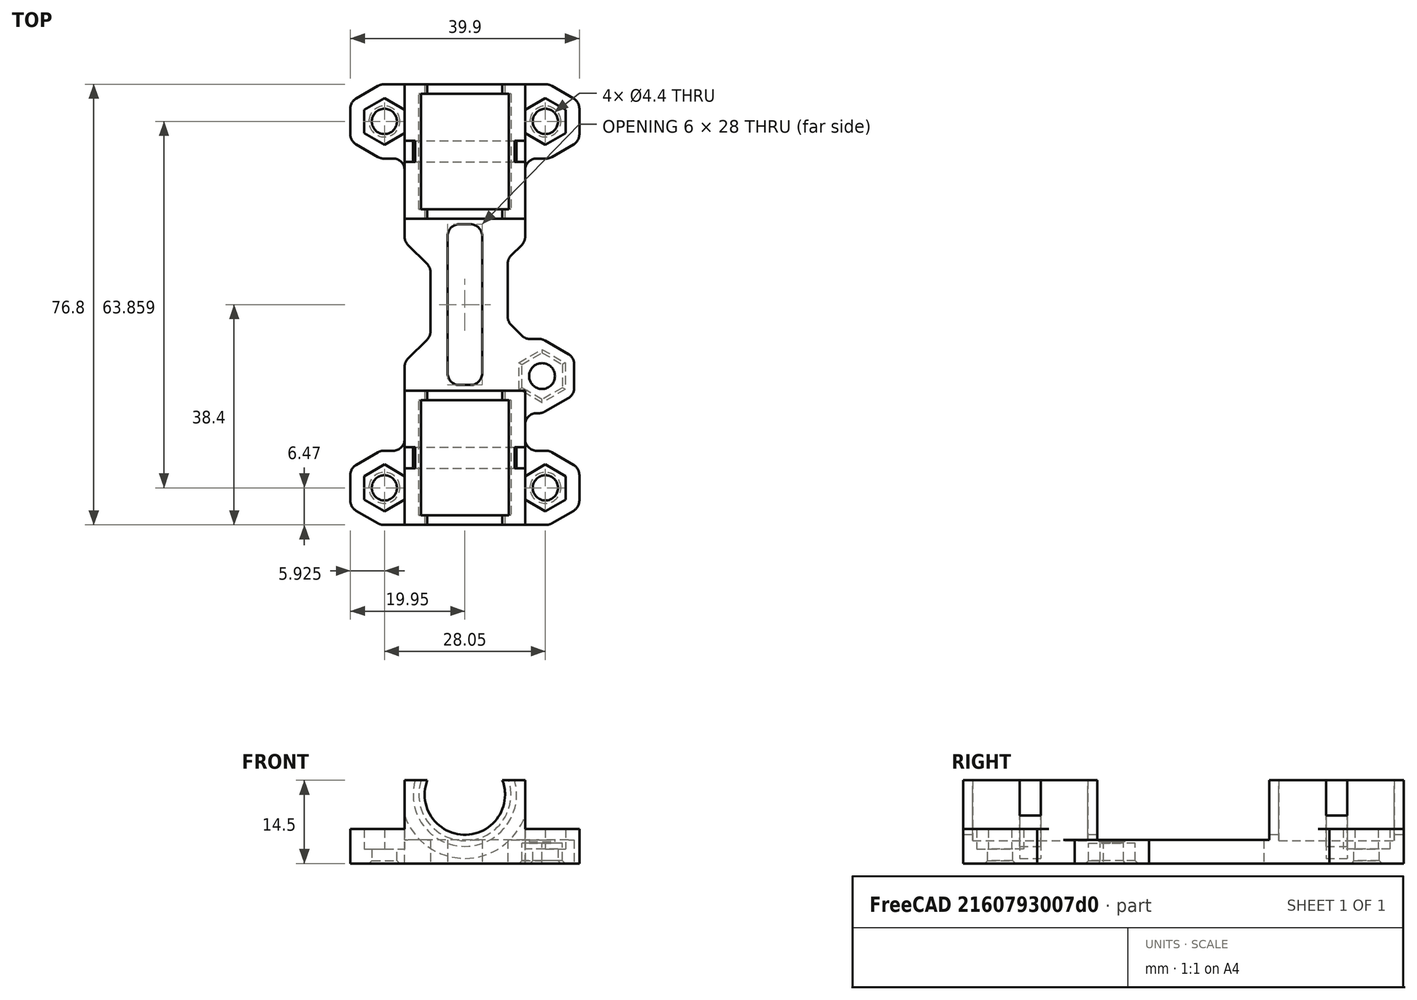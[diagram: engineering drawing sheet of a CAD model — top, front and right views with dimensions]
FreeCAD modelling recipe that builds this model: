
FCSTD DOCUMENT  (FreeCAD 0.15R4671 (Git))
Label: Halter Gleitlager Z - Zusammenbau rechts
License: All rights reserved
LicenseURL: http://de.wikipedia.org/wiki/Alle_Rechte_vorbehalten
objects: Part::FeaturePython×7, Part::MultiFuse×1, PartDesign::Chamfer×1, PartDesign::Fillet×1
note: 10 computed .brp shape members not serialized (recipe doc carries the construction recipe); baked Part::Feature solids carry a one-line shape summary decoded from their .brp

FEATURE [Part::FeaturePython] Halter_Gleitlager_Z___Gleitlager_01  # a2plus imported part (geometry in sourceFile) (typed FeaturePython)
  Placement = pos=(0,26.2,0) rot=(0,0,1;0rad)
  fixedPosition = false
  sourceFile = <path> Gleitlager Z - Gleitlager.FCStd
  timeLastImport = 1.45545e+09
  updateColors = true
FEATURE [Part::FeaturePython] Halter_Gleitlager_Z___Gleitlager_01001  # a2plus imported part (geometry in sourceFile) (typed FeaturePython)
  Placement = pos=(0,-27.2,0) rot=(0,0,1;0rad)
  fixedPosition = false
  sourceFile = <path> Gleitlager Z - Gleitlager.FCStd
  timeLastImport = 1.45545e+09
  updateColors = true
FEATURE [Part::FeaturePython] Halter_Gleitlager_Z___Verschraubung_01  # a2plus imported part (geometry in sourceFile) (typed FeaturePython)
  Placement = pos=(14.025,31.4297,0) rot=(0,0,1;0rad)
  fixedPosition = false
  sourceFile = <path> Gleitlager Z - Verschraubung.FCStd
  timeLastImport = 1.45539e+09
  updateColors = true
FEATURE [Part::FeaturePython] Halter_Gleitlager_Z___Verschraubung_01001  # a2plus imported part (geometry in sourceFile) (typed FeaturePython)
  Placement = pos=(14.025,-32.4297,0) rot=(0,0,1;0rad)
  fixedPosition = false
  sourceFile = <path> Gleitlager Z - Verschraubung.FCStd
  timeLastImport = 1.45539e+09
  updateColors = true
FEATURE [Part::FeaturePython] Halter_Gleitlager_Z___Verschraubung_  # a2plus imported part (geometry in sourceFile) (typed FeaturePython)
  Placement = pos=(-14.025,-32.4297,0) rot=(0,0,1;3.14159rad)
  fixedPosition = false
  sourceFile = <path> Gleitlager Z - Verschraubung.FCStd
  timeLastImport = 1.45539e+09
  updateColors = true
FEATURE [Part::FeaturePython] Halter_Gleitlager_Z___Verschraubung_01002  # a2plus imported part (geometry in sourceFile) (typed FeaturePython)
  Placement = pos=(-14.025,31.4297,0) rot=(0,0,1;3.14159rad)
  fixedPosition = false
  sourceFile = <path> Gleitlager Z - Verschraubung.FCStd
  timeLastImport = 1.45539e+09
  updateColors = true
FEATURE [Part::FeaturePython] Halter_Gleitlager_Z___Zwischenstueck_rechts_  # a2plus imported part (geometry in sourceFile) (typed FeaturePython)
  Placement = pos=(0,0,4.1) rot=(0,1,0;3.14159rad)
  fixedPosition = true
  sourceFile = <path> Gleitlager Z - Zwischenstueck rechts.FCStd
  timeLastImport = 1.45546e+09
  updateColors = true
FEATURE [Part::MultiFuse] Fusion
  Shapes = -> [Halter_Gleitlager_Z___Zwischenstueck_rechts_,Halter_Gleitlager_Z___Verschraubung_01002,Halter_Gleitlager_Z___Gleitlager_01,Halter_Gleitlager_Z___Verschraubung_01001,Halter_Gleitlager_Z___Verschraubung_01,Halter_Gleitlager_Z___Gleitlager_01001,Halter_Gleitlager_Z___Verschraubung_]
FEATURE [PartDesign::Chamfer] Chamfer
  Base = -> Fusion [Edge120,Edge119,Edge121,Edge123,Edge124,Edge122,Edge129,Edge14,Edge256,Edge263]
  Size = 0.5
FEATURE [PartDesign::Fillet] Fillet
  Base = -> Chamfer [Edge189,Edge222,Edge221,Edge81,Edge114,Edge118,Edge122,Edge135,Edge157,Edge139,Edge246,Edge331,Edge359,Edge358,Edge82,Edge201,Edge126,Edge130,Edge133,Edge357,Edge161,Edge350,Edge352,Edge348,Edge152,Edge145,Edge141,Edge137,Edge21,Edge23,Edge26,Edge24,Edge156,Edge18,Edge159,Edge268,Edge346]
  Radius = 2
note: 7 file-system paths scrubbed to <path> (originals preserved in the JSON sidecar)
